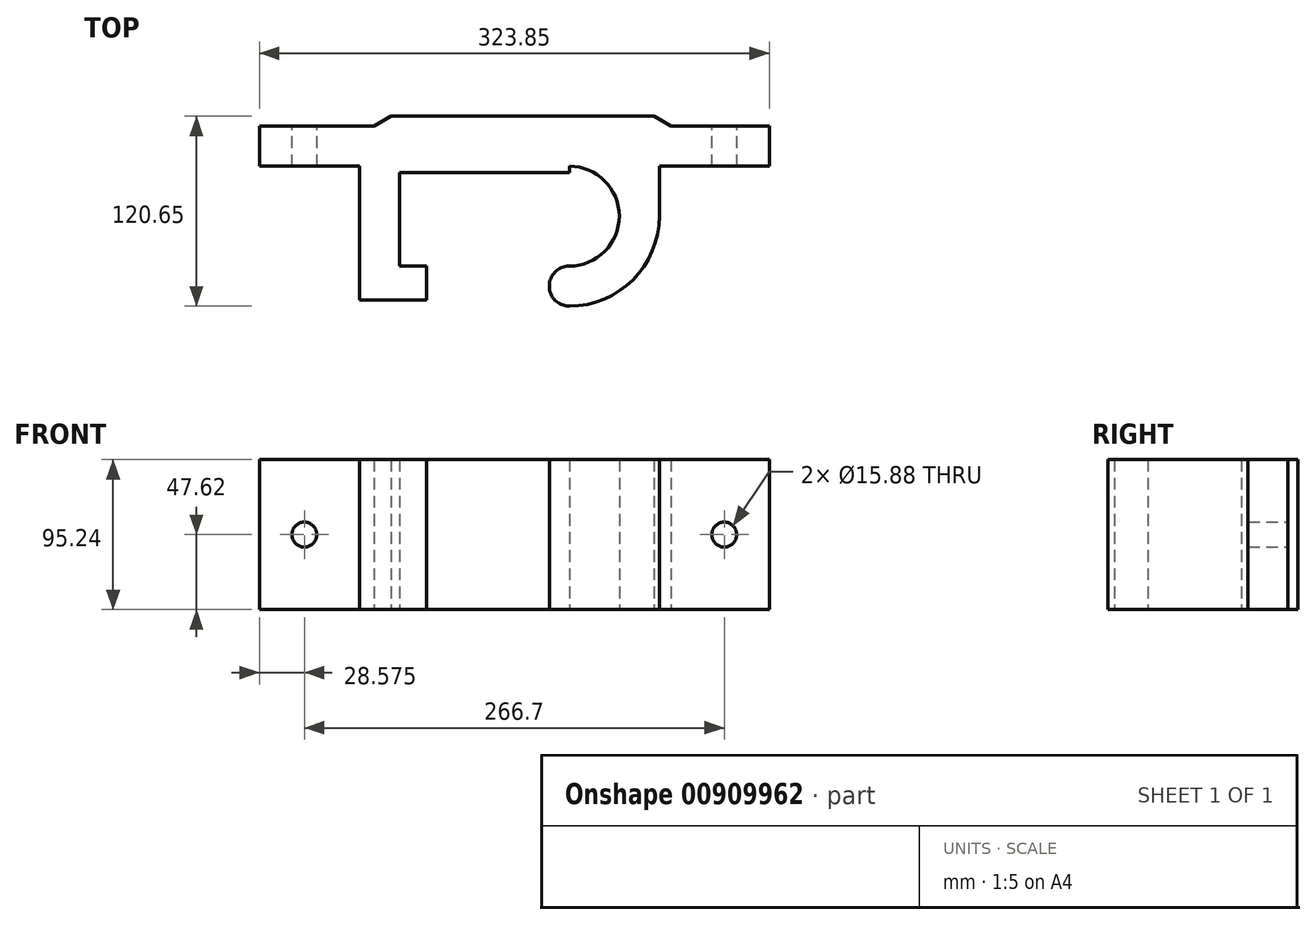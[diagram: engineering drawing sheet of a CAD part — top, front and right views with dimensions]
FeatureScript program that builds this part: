
annotation { "Feature Type Name" : "Feature", "Feature Type Description" : "" }
export const myFeature = defineFeature(function(context is Context, id is Id, definition is map)
    precondition{}
    {
        {
            var Q0;
            Q0=qCreatedBy(makeId("Top.planeOp"),FACE);
            var sketch = newSketch(context, id + "F0", { "sketchPlane" : qUnion([Q0])});
            skArc(sketch, "E0", {"start": v(0, -31.75) * mm, "mid": v(31.75, 0) * mm, "end": v(0, 31.75) * mm});
            skArc(sketch, "E1", {"start": v(0, -57.15) * mm, "mid": v(40.41, -40.41) * mm, "end": v(57.15, 0) * mm});
            skLineSegment(sketch, "E2", {"start": v(0, 31.75) * mm, "end": v(0, 27.61) * mm});
            skLineSegment(sketch, "E3", {"start": v(0, 27.61) * mm, "end": v(-107.95, 27.61) * mm});
            skLineSegment(sketch, "E4", {"start": v(-107.95, 27.61) * mm, "end": v(-107.95, -31.75) * mm});
            skLineSegment(sketch, "E5", {"start": v(-107.95, -31.75) * mm, "end": v(-90.5, -31.75) * mm});
            skLineSegment(sketch, "E6", {"start": v(-90.5, -31.75) * mm, "end": v(-90.5, -53.1) * mm});
            skLineSegment(sketch, "E7", {"start": v(-90.5, -53.1) * mm, "end": v(-133.35, -53.1) * mm});
            skLineSegment(sketch, "E8", {"start": v(-133.35, -53.1) * mm, "end": v(-133.35, 31.75) * mm});
            skLineSegment(sketch, "E9", {"start": v(-133.35, 31.75) * mm, "end": v(-196.85, 31.75) * mm});
            skLineSegment(sketch, "E10", {"start": v(-196.85, 31.75) * mm, "end": v(-196.85, 57.15) * mm});
            skLineSegment(sketch, "E11", {"start": v(-196.85, 57.15) * mm, "end": v(-124.02, 57.15) * mm});
            skLineSegment(sketch, "E12", {"start": v(-124.02, 57.15) * mm, "end": v(-113.28, 63.5) * mm});
            skLineSegment(sketch, "E13", {"start": v(-113.28, 63.5) * mm, "end": v(53.84, 63.5) * mm});
            skLineSegment(sketch, "E14", {"start": v(53.84, 63.5) * mm, "end": v(64.51, 57.15) * mm});
            skLineSegment(sketch, "E15", {"start": v(64.51, 57.15) * mm, "end": v(127, 57.15) * mm});
            skLineSegment(sketch, "E16", {"start": v(127, 57.15) * mm, "end": v(127, 31.75) * mm});
            skLineSegment(sketch, "E17", {"start": v(127, 31.75) * mm, "end": v(57.15, 31.75) * mm});
            skArc(sketch, "E18", {"start": v(0, -31.75) * mm, "mid": v(-12.7, -44.45) * mm, "end": v(0, -57.15) * mm});
            skLineSegment(sketch, "E19", {"start": v(57.15, 0) * mm, "end": v(57.15, 31.75) * mm});
            skSolve(sketch);
        }
        {
            var Q0;
            Q0=makeQuery(id+"F0.imprint","IMPRINT",FACE,{"disambiguationData":[TD([[makeQuery(id+"F0.imprint","IMPRINT",EDGE,{"derivedFrom":sQuery(id+"F0.wireOp",EDGE,"E0")}),-1.0]])]});
            extrude(context, id + "F1", {"entities" : qUnion([Q0]), "depth" : 95.25 * mm, "offsetDistance" : 25 * mm, "symmetric" : true});
        }
        {
            var Q0;
            Q0=makeQuery(id+"F1.opExtrude","SWEPT_FACE",FACE,{"disambiguationData":[OSD([sQuery(id+"F0.wireOp",EDGE,"E15")])]});
            var sketch = newSketch(context, id + "F2", { "sketchPlane" : qUnion([Q0])});
            skCircle(sketch, "E20", {"center": v(-98.42, 0) * mm, "radius": 7.94 * mm});
            skCircle(sketch, "E21", {"center": v(168.27, 0) * mm, "radius": 7.94 * mm});
            skLineSegment(sketch, "E22", {"start": v(-98.43, 0) * mm, "end": v(168.27, 0) * mm, "construction": true});
            skLineSegment(sketch, "E23", {"start": v(-127, 0) * mm, "end": v(-98.42, 0) * mm, "construction": true});
            skSolve(sketch);
        }
        {
            var Q0;
            Q0=makeQuery(id+"F2.imprint","IMPRINT",FACE,{"disambiguationData":[TD([[makeQuery(id+"F2.imprint","IMPRINT",EDGE,{"derivedFrom":sQuery(id+"F2.wireOp",EDGE,"E20")}),1.0]])]});
            var Q1;
            Q1=makeQuery(id+"F2.imprint","IMPRINT",FACE,{"disambiguationData":[TD([[makeQuery(id+"F2.imprint","IMPRINT",EDGE,{"derivedFrom":sQuery(id+"F2.wireOp",EDGE,"E21")}),1.0]])]});
            extrude(context, id + "F3", {"entities" : qUnion([Q0, Q1]), "operationType" : NewBodyOperationType.REMOVE, "endBound" : BoundingType.THROUGH_ALL, "oppositeDirection" : true, "depth" : 25 * mm, "offsetDistance" : 25 * mm});
        }
    });
